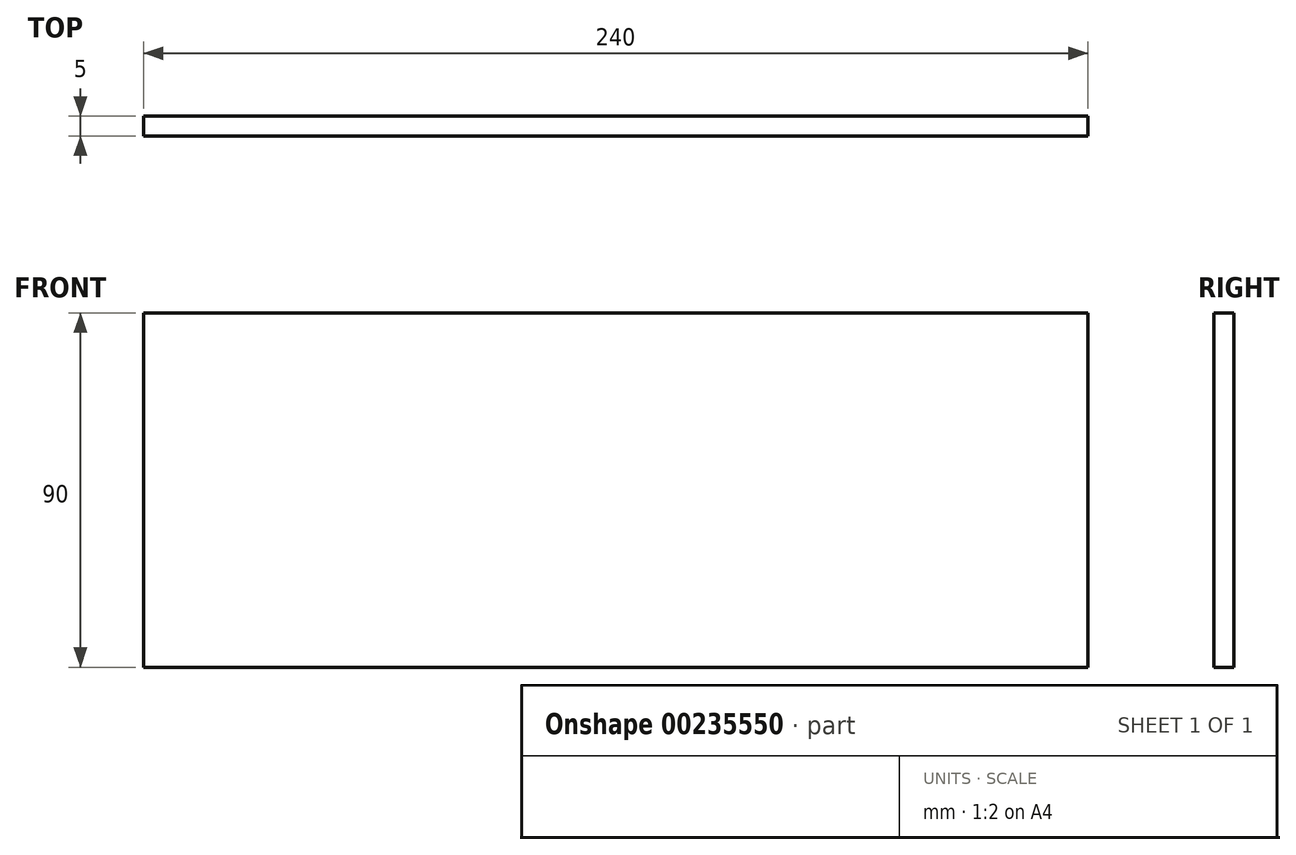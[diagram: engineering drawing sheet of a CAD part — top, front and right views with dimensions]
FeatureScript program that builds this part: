
annotation { "Feature Type Name" : "Feature", "Feature Type Description" : "" }
export const myFeature = defineFeature(function(context is Context, id is Id, definition is map)
    precondition{}
    {
        {
            var Q0;
            Q0=qCreatedBy(makeId("Front.planeOp"),FACE);
            var sketch = newSketch(context, id + "F0", { "sketchPlane" : qUnion([Q0])});
            skLineSegment(sketch, "E0.bottom", {"start": v(120, -45) * mm, "end": v(-120, -45) * mm});
            skLineSegment(sketch, "E0.top", {"start": v(120, 45) * mm, "end": v(-120, 45) * mm});
            skLineSegment(sketch, "E0.left", {"start": v(120, -45) * mm, "end": v(120, 45) * mm});
            skLineSegment(sketch, "E0.right", {"start": v(-120, -45) * mm, "end": v(-120, 45) * mm});
            skPoint(sketch, "E0.middle", {"position": v(0, 0) * mm});
            skSolve(sketch);
        }
        {
            var Q0;
            Q0=qSketchRegion(id+"F0",true);
            extrude(context, id + "F1", {"entities" : qUnion([Q0]), "depth" : 5 * mm});
        }
    });
